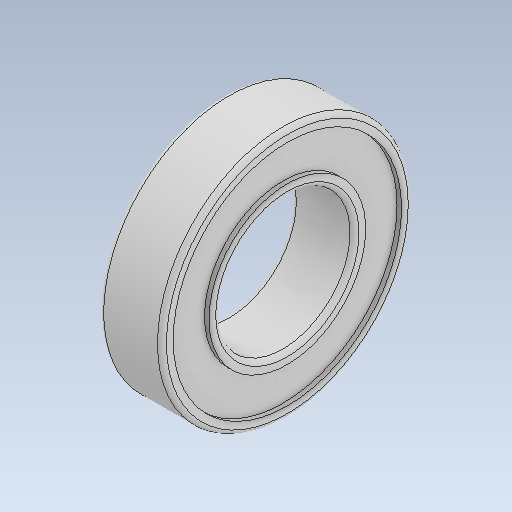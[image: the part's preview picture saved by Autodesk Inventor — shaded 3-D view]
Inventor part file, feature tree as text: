
AUTODESK INVENTOR PART (.ipt)
format: ipt  version: 2020 (Build 240168000, 168)  size: 179,200 bytes
history: native  units: in
note: dims shown in document units (in); Inventor stores cm internally (conversion verified against a paired STEP export)
features: fillet x1
ambient origin geometry x8: Origin, YZ Plane, XZ Plane, XY Plane, X Axis, Y Axis, Z Axis, Center Point
bodies: Solid1 (feature_tree)
feature tree (1):
  fillet  "Fillet1"  [1 undecoded]
note: 1 required parameter value undecoded (feature->parameter linkage not recoverable at this tier; creation-order binding heuristic only, values carry confidence <= 0.55)
